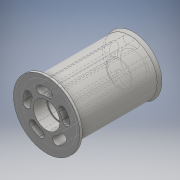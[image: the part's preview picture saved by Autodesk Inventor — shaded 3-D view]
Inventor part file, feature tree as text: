
AUTODESK INVENTOR PART (.ipt)
format: ipt  version: 2016 (Build 200138000, 138)  size: 199,168 bytes
history: native  units: mm
features: extrude x7, sketch x7, projected_geometry x3, fillet x1
ambient origin geometry x8: Origin, YZ Plane, XZ Plane, XY Plane, X Axis, Y Axis, Z Axis, Center Point
bodies: Solid1 (feature_tree)
feature tree (18):
  extrude  "Extrusion1"  Depth=56.0mm
  extrude  "Extrusion2"  Depth=2.0mm
  extrude  "Extrusion3"  Depth=3.0mm
  extrude  "Extrusion4"  Depth=20.0mm
  extrude  "Extrusion5"  Depth=22.1mm
  extrude  "Extrusion6"  Depth=12.0mm
  extrude  "Extrusion7"  Depth=0.5mm
  fillet  "Fillet1"  Radius=60.0mm
  sketch  "Sketch1"  dims[d0=22.1mm d1=56.0mm]
  sketch  "Sketch2"  dims[d2=2.0mm d3=0.0mm d4=46.0mm]
  sketch  "Sketch3"  dims[d5=68.0mm d6=0.0mm d7=3.0mm d8=3.490659mm]
  projected_geometry  "Projected Loop1"
  sketch  "Sketch4"  dims[d9=9.0mm d10=0.0mm d11=20.0mm]
  projected_geometry  "Projected Loop2"
  sketch  "Sketch5"  dims[d12=7.0mm d13=0.0mm d14=22.1mm]
  sketch  "Sketch6"  dims[d15=12.0mm d16=0.0mm d17=27.0mm]
  sketch  "Sketch7"  dims[d18=40.0mm d19=24.43461mm d20=60.0mm d22=6.981317mm d24=50.0mm d26=360.0deg d28=12.0mm d29=0.0mm d30=0.5mm]
  projected_geometry  "Projected Loop3"
